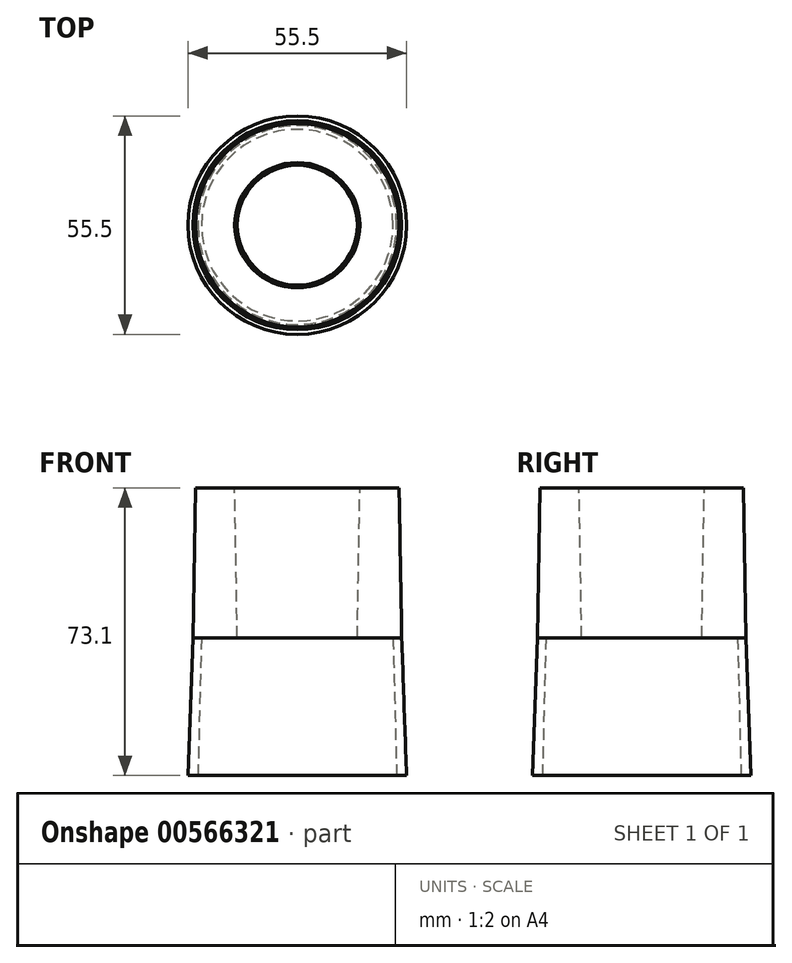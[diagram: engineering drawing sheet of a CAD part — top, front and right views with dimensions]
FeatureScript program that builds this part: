
annotation { "Feature Type Name" : "Feature", "Feature Type Description" : "" }
export const myFeature = defineFeature(function(context is Context, id is Id, definition is map)
    precondition{}
    {
        {
            var Q0;
            Q0=qCreatedBy(makeId("Top.planeOp"),FACE);
            var sketch = newSketch(context, id + "F0", { "sketchPlane" : qUnion([Q0])});
            skCircle(sketch, "E0", {"center": v(0, 0) * mm, "radius": 27.75 * mm});
            skSolve(sketch);
        }
        {
            var Q0;
            Q0 = qSketchRegion(id + "F0", true);
            extrude(context, id + "F1", {"entities" : qUnion([Q0]), "depth" : 35 * mm, "offsetDistance" : 25.4 * mm, "hasDraft" : true, "draftAngle" : 2 * degree, "draftPullDirection" : true});
        }
        {
            var Q0;
            Q0=makeQuery(id+"F1.opExtrude","CAP_FACE",FACE,{"disambiguationData":[OSD([sQuery(id+"F0.wireOp",EDGE,"E0")])],"isStart":true});
            var sketch = newSketch(context, id + "F2", { "sketchPlane" : qUnion([Q0])});
            skCircle(sketch, "E1", {"center": v(0, 0) * mm, "radius": 25.25 * mm});
            skSolve(sketch);
        }
        {
            var Q0;
            Q0=makeQuery(id+"F2.imprint","IMPRINT",FACE,{"disambiguationData":[TD([[makeQuery(id+"F2.imprint","IMPRINT",EDGE,{"derivedFrom":sQuery(id+"F2.wireOp",EDGE,"E1")}),1.0]])]});
            extrude(context, id + "F3", {"entities" : qUnion([Q0]), "operationType" : NewBodyOperationType.REMOVE, "endBound" : BoundingType.THROUGH_ALL, "oppositeDirection" : true, "depth" : 25.4 * mm, "offsetDistance" : 25.4 * mm, "hasDraft" : true, "draftAngle" : 1.5 * degree, "draftPullDirection" : true});
        }
        {
            var Q0;
            Q0=makeQuery(id+"F1.opExtrude","CAP_FACE",FACE,{"disambiguationData":[OSD([sQuery(id+"F0.wireOp",EDGE,"E0")])],"isStart":false});
            var sketch = newSketch(context, id + "F4", { "sketchPlane" : qUnion([Q0])});
            skCircle(sketch, "E2", {"center": v(0, 0) * mm, "radius": 26.53 * mm});
            skCircle(sketch, "E3", {"center": v(0, 0) * mm, "radius": 15.24 * mm});
            skSolve(sketch);
        }
        {
            var Q0;
            Q0 = qSketchRegion(id + "F4", true);
            extrude(context, id + "F5", {"entities" : qUnion([Q0]), "operationType" : NewBodyOperationType.ADD, "depth" : 38.1 * mm, "offsetDistance" : 25.4 * mm, "hasDraft" : true, "draftAngle" : 1 * degree, "draftPullDirection" : true});
        }
    });
